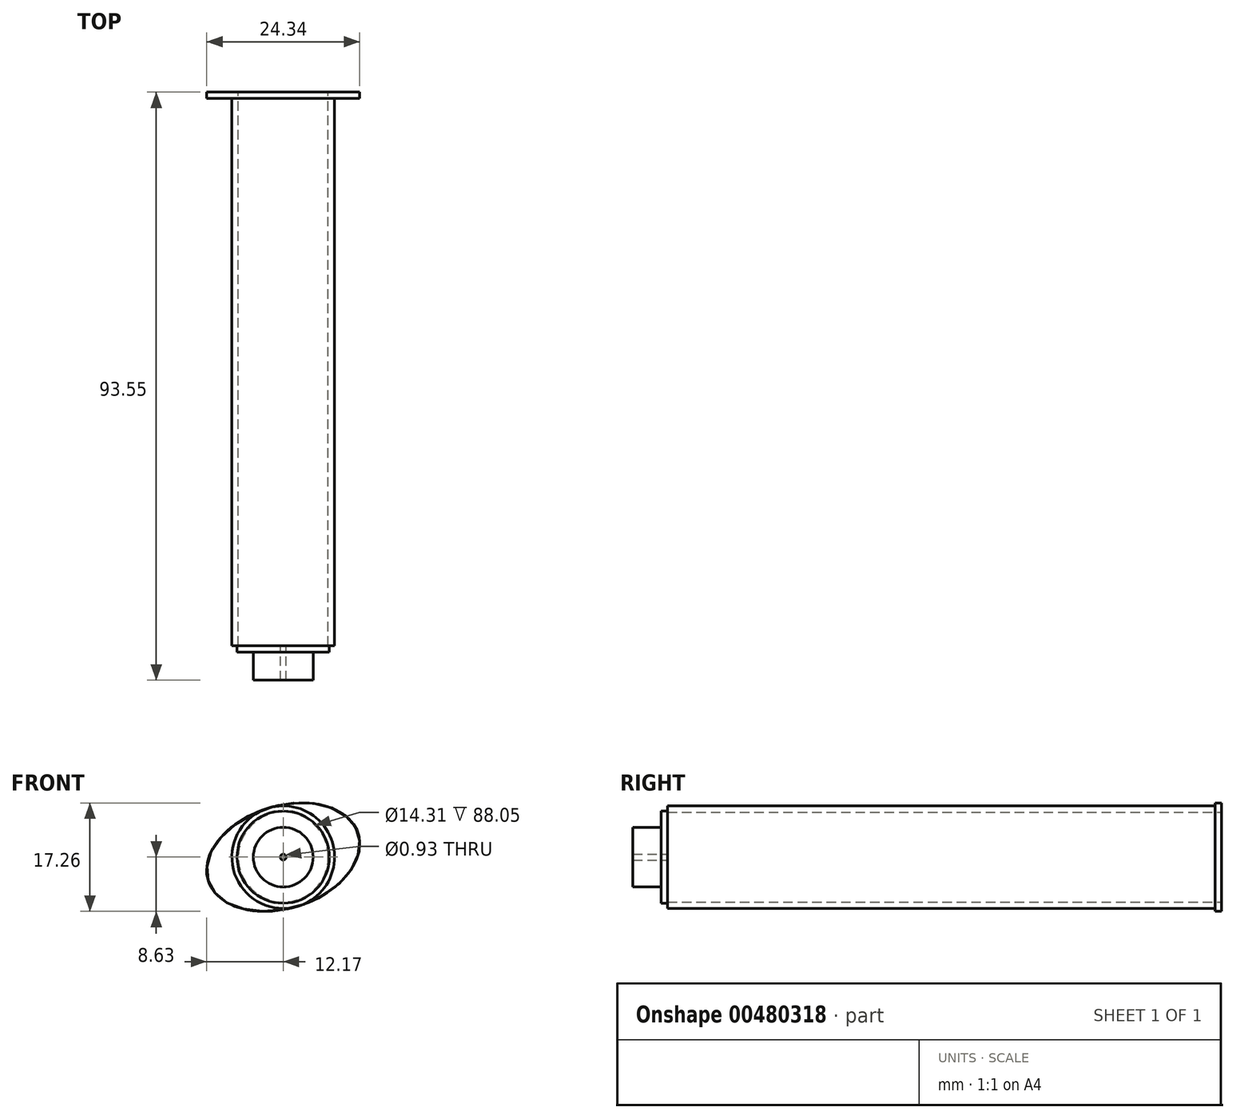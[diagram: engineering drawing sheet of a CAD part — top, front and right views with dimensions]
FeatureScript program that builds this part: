
annotation { "Feature Type Name" : "Feature", "Feature Type Description" : "" }
export const myFeature = defineFeature(function(context is Context, id is Id, definition is map)
    precondition{}
    {
        {
            var Q0;
            Q0=qCreatedBy(makeId("Front.planeOp"),FACE);
            var sketch = newSketch(context, id + "F0", { "sketchPlane" : qUnion([Q0])});
            skCircle(sketch, "E0", {"center": v(0, 0) * mm, "radius": 7.16 * mm});
            skCircle(sketch, "E1.0", {"center": v(0, 0) * mm, "radius": 8.16 * mm});
            skEllipse(sketch, "E2", {"center": v(0, 0) * mm, "majorRadius": 12.5 * mm, "minorRadius": 8.16 * mm, "majorAxis": v(-0.95, -0.3)});
            skSolve(sketch);
        }
        {
            var Q0;
            Q0=makeQuery(id+"F0.imprint","IMPRINT",FACE,{"disambiguationData":[TD([[makeQuery(id+"F0.imprint","IMPRINT",EDGE,{"derivedFrom":sQuery(id+"F0.wireOp",EDGE,"E0")}),-1.0]])]});
            extrude(context, id + "F1", {"entities" : qUnion([Q0]), "depth" : 88.05 * mm});
        }
        {
            var Q0;
            {var subQ0=sQuery(id+"F0.wireOp",EDGE,"E2");var subQ1=sQuery(id+"F0.wireOp",EDGE,"E1.0");var subQ2=makeQuery(id+"F0.imprint","INTERSECT",VERTEX,{"disambiguationData":[OD(0.0)],"derivedFrom":[subQ1,subQ0]});Q0=makeQuery(id+"F0.imprint","IMPRINT",FACE,{"disambiguationData":[TD([[makeQuery(id+"F0.imprint","IMPRINT",EDGE,{"disambiguationData":[TD([[subQ2,1.0]])],"derivedFrom":subQ1}),-1.0]])]});}
            var Q1;
            {var subQ0=sQuery(id+"F0.wireOp",EDGE,"E2");var subQ1=sQuery(id+"F0.wireOp",EDGE,"E1.0");var subQ2=makeQuery(id+"F0.imprint","INTERSECT",VERTEX,{"disambiguationData":[OD(0.0)],"derivedFrom":[subQ1,subQ0]});Q1=makeQuery(id+"F0.imprint","IMPRINT",FACE,{"disambiguationData":[TD([[makeQuery(id+"F0.imprint","IMPRINT",EDGE,{"disambiguationData":[TD([[subQ2,-1.0]])],"derivedFrom":subQ1}),-1.0]])]});}
            extrude(context, id + "F2", {"entities" : qUnion([Q0, Q1]), "operationType" : NewBodyOperationType.ADD, "depth" : 1 * mm});
        }
        {
            var Q0;
            Q0=makeQuery(id+"F1.opExtrude","CAP_FACE",FACE,{"disambiguationData":[OSD([sQuery(id+"F0.wireOp",EDGE,"E0"),sQuery(id+"F0.wireOp",EDGE,"E1.0")])],"isStart":false});
            var sketch = newSketch(context, id + "F3", { "sketchPlane" : qUnion([Q0])});
            skCircle(sketch, "E3.0", {"center": v(0, 0) * mm, "radius": 8.16 * mm});
            skCircle(sketch, "E4", {"center": v(0, 0) * mm, "radius": 7.33 * mm});
            skCircle(sketch, "E5", {"center": v(0, 0) * mm, "radius": 4.75 * mm});
            skCircle(sketch, "E6", {"center": v(0, 0) * mm, "radius": 0.46 * mm});
            skSolve(sketch);
        }
        {
            var Q0;
            Q0=makeQuery(id+"F3.imprint","IMPRINT",FACE,{"disambiguationData":[TD([[makeQuery(id+"F3.imprint","IMPRINT",EDGE,{"derivedFrom":sQuery(id+"F3.wireOp",EDGE,"E4")}),1.0]])]});
            var Q1;
            Q1=makeQuery(id+"F3.imprint","IMPRINT",FACE,{"disambiguationData":[TD([[makeQuery(id+"F3.imprint","IMPRINT",EDGE,{"derivedFrom":makeQuery(id+"F1.opExtrude","CAP_EDGE",EDGE,{"disambiguationData":[OSD([sQuery(id+"F0.wireOp",EDGE,"E0")])],"isStart":false})}),1.0]])]});
            extrude(context, id + "F4", {"entities" : qUnion([Q0, Q1]), "operationType" : NewBodyOperationType.ADD, "depth" : 1 * mm});
        }
        {
            var Q0;
            Q0=makeQuery(id+"F3.imprint","IMPRINT",FACE,{"disambiguationData":[TD([[makeQuery(id+"F3.imprint","IMPRINT",EDGE,{"derivedFrom":sQuery(id+"F3.wireOp",EDGE,"E5")}),1.0]])]});
            extrude(context, id + "F5", {"entities" : qUnion([Q0]), "operationType" : NewBodyOperationType.ADD, "depth" : 5.5 * mm});
        }
    });
